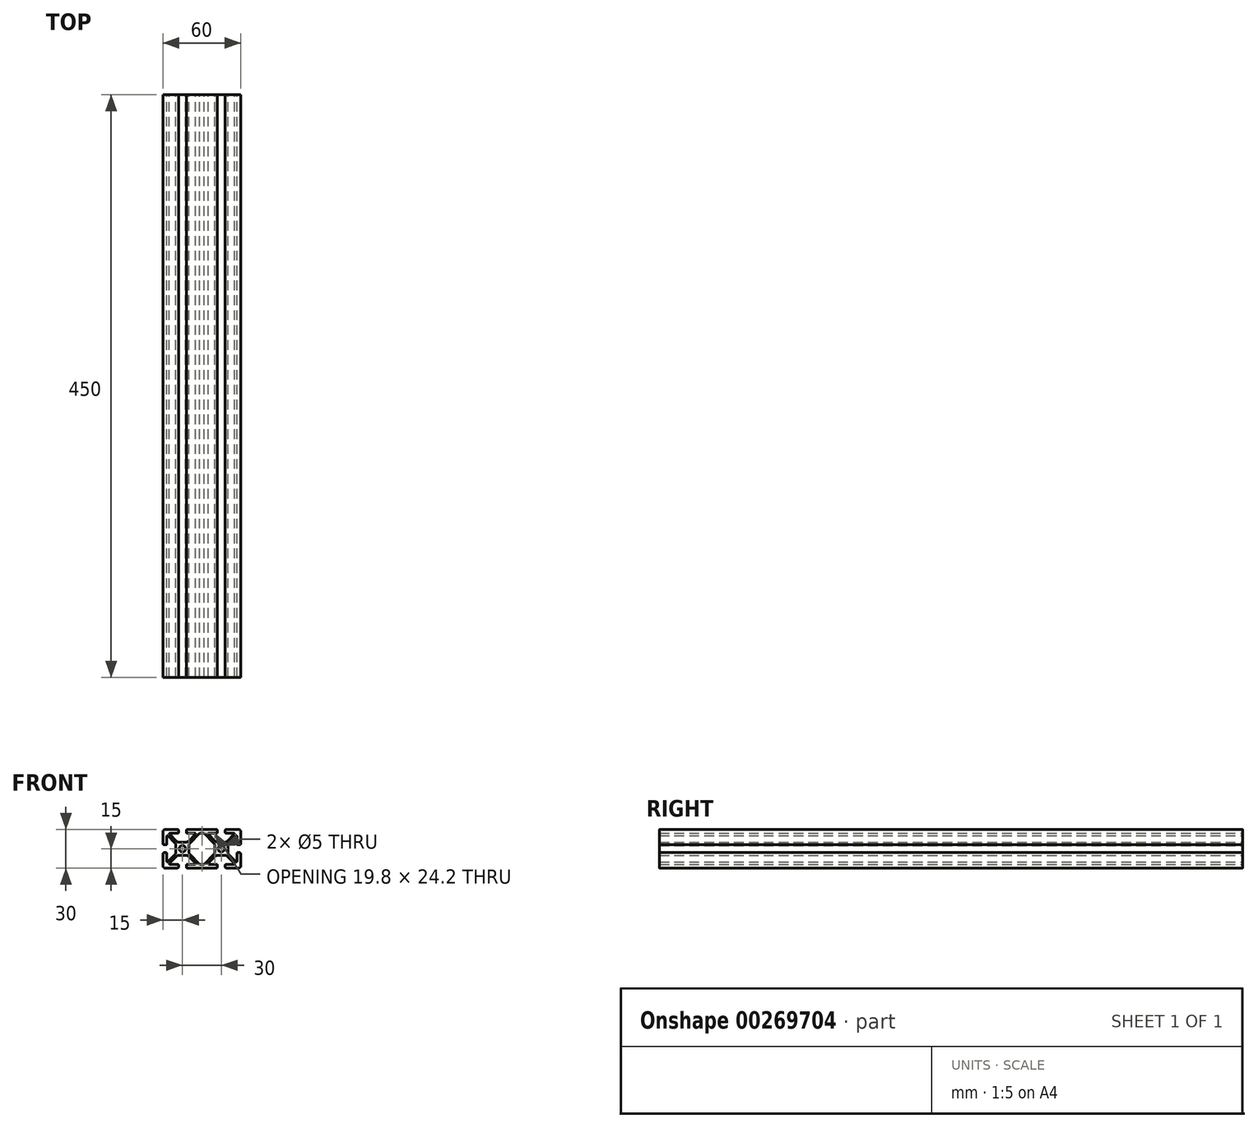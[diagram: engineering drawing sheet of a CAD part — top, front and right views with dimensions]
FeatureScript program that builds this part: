
annotation { "Feature Type Name" : "Feature", "Feature Type Description" : "" }
export const myFeature = defineFeature(function(context is Context, id is Id, definition is map)
    precondition{}
    {
        {
            var Q0;
            Q0=qCreatedBy(makeId("Front.planeOp"),FACE);
            var sketch = newSketch(context, id + "F0", { "sketchPlane" : qUnion([Q0])});
            skLineSegment(sketch, "E0.top", {"start": v(-28.2, -15) * mm, "end": v(-19, -15) * mm});
            skCircle(sketch, "E1", {"center": v(-15, 0) * mm, "radius": 2.5 * mm});
            skLineSegment(sketch, "E2", {"start": v(-15, 0) * mm, "end": v(15, 0) * mm, "construction": true});
            skLineSegment(sketch, "E3", {"start": v(-24.62, -12.1) * mm, "end": v(-18.5, -12.1) * mm});
            skLineSegment(sketch, "E4", {"start": v(-15, 0) * mm, "end": v(-15, -15) * mm, "construction": true});
            skLineSegment(sketch, "E5.bottom", {"start": v(-12.2, -5.1) * mm, "end": v(-17.8, -5.1) * mm});
            skLineSegment(sketch, "E6.trimOffspring", {"start": v(-18, -12.6) * mm, "end": v(-18, -14) * mm});
            skLineSegment(sketch, "E7.trimOffspring", {"start": v(-12, -12.6) * mm, "end": v(-12, -14) * mm});
            skLineSegment(sketch, "E8.trimOffspring", {"start": v(-11.5, -12.1) * mm, "end": v(-5.38, -12.1) * mm});
            skLineSegment(sketch, "E9.0", {"start": v(-26.25, -9.97) * mm, "end": v(-20.83, -4.56) * mm});
            skLineSegment(sketch, "E10.trimOffspring", {"start": v(-24.97, -11.25) * mm, "end": v(-19.56, -5.83) * mm});
            skLineSegment(sketch, "E11", {"start": v(-15, 0) * mm, "end": v(-30, -15) * mm, "construction": true});
            skLineSegment(sketch, "E12.MirrorCS", {"start": v(-27.1, -9.62) * mm, "end": v(-27.1, -3.5) * mm});
            skLineSegment(sketch, "E13.MirrorCS", {"start": v(-27.6, -3) * mm, "end": v(-29, -3) * mm});
            skLineSegment(sketch, "E14.MirrorCS", {"start": v(-5.03, -11.25) * mm, "end": v(-10.44, -5.83) * mm});
            skLineSegment(sketch, "E15.MirrorCS", {"start": v(-1.63, -12.1) * mm, "end": v(-9.17, -4.56) * mm});
            skLineSegment(sketch, "E16.trimOffspring", {"start": v(-30, -4) * mm, "end": v(-30, -13.2) * mm});
            skPoint(sketch, "E17.visualSharp", {"position": v(-30, -15) * mm});
            skArc(sketch, "E17.filletArc", {"start": v(-30, -13.2) * mm, "mid": v(-29.47, -14.47) * mm, "end": v(-28.2, -15) * mm});
            skPoint(sketch, "E18.visualSharp", {"position": v(-18, -15) * mm});
            skArc(sketch, "E18.filletArc", {"start": v(-19, -15) * mm, "mid": v(-18.3, -14.7) * mm, "end": v(-18, -14) * mm});
            skLineSegment(sketch, "E19", {"start": v(-18, -14) * mm, "end": v(-12, -14) * mm, "construction": true});
            skPoint(sketch, "E20", {"position": v(-15, -14) * mm});
            skPoint(sketch, "E21.orphan", {"position": v(-28.9, -5.1) * mm});
            skPoint(sketch, "E22.visualSharp", {"position": v(-18.83, -5.1) * mm});
            skArc(sketch, "E22.filletArc", {"start": v(-17.8, -5.1) * mm, "mid": v(-18.75, -5.3) * mm, "end": v(-19.56, -5.83) * mm});
            skPoint(sketch, "E23.visualSharp", {"position": v(-11.17, -5.1) * mm});
            skArc(sketch, "E23.filletArc", {"start": v(-10.44, -5.83) * mm, "mid": v(-11.25, -5.3) * mm, "end": v(-12.2, -5.1) * mm});
            skPoint(sketch, "E24.visualSharp", {"position": v(-23.4, -7.14) * mm});
            skArc(sketch, "E24.filletArc", {"start": v(-20.83, -4.56) * mm, "mid": v(-20.3, -3.75) * mm, "end": v(-20.1, -2.8) * mm});
            skPoint(sketch, "E25.visualSharp", {"position": v(-6.6, -7.14) * mm});
            skPoint(sketch, "E26.visualSharp", {"position": v(-12, -15) * mm});
            skArc(sketch, "E26.filletArc", {"start": v(-12, -14) * mm, "mid": v(-11.7, -14.7) * mm, "end": v(-11, -15) * mm});
            skPoint(sketch, "E27.visualSharp", {"position": v(-12, -12.1) * mm});
            skArc(sketch, "E27.filletArc", {"start": v(-11.5, -12.1) * mm, "mid": v(-11.85, -12.25) * mm, "end": v(-12, -12.6) * mm});
            skPoint(sketch, "E28.visualSharp", {"position": v(-18, -12.1) * mm});
            skArc(sketch, "E28.filletArc", {"start": v(-18, -12.6) * mm, "mid": v(-18.15, -12.25) * mm, "end": v(-18.5, -12.1) * mm});
            skPoint(sketch, "E29.visualSharp", {"position": v(-27.1, -3) * mm});
            skArc(sketch, "E29.filletArc", {"start": v(-27.1, -3.5) * mm, "mid": v(-27.25, -3.15) * mm, "end": v(-27.6, -3) * mm});
            skPoint(sketch, "E30.visualSharp", {"position": v(-30, -3) * mm});
            skArc(sketch, "E30.filletArc", {"start": v(-29, -3) * mm, "mid": v(-29.7, -3.3) * mm, "end": v(-30, -4) * mm});
            skPoint(sketch, "E31.visualSharp", {"position": v(-27.1, -10.83) * mm});
            skArc(sketch, "E31.filletArc", {"start": v(-27.1, -9.62) * mm, "mid": v(-26.8, -10.08) * mm, "end": v(-26.25, -9.97) * mm});
            skPoint(sketch, "E32.visualSharp", {"position": v(-25.83, -12.1) * mm});
            skArc(sketch, "E32.filletArc", {"start": v(-24.97, -11.25) * mm, "mid": v(-25.08, -11.8) * mm, "end": v(-24.62, -12.1) * mm});
            skPoint(sketch, "E33.visualSharp", {"position": v(-4.17, -12.1) * mm});
            skArc(sketch, "E33.filletArc", {"start": v(-5.38, -12.1) * mm, "mid": v(-4.92, -11.8) * mm, "end": v(-5.03, -11.25) * mm});
            skLineSegment(sketch, "E34", {"start": v(-10.44, 5.83) * mm, "end": v(-9.17, 4.56) * mm, "construction": true});
            skPoint(sketch, "E35", {"position": v(-9.8, 5.2) * mm});
            skLineSegment(sketch, "E36.MirrorCS", {"start": v(-28.2, 15) * mm, "end": v(-19, 15) * mm});
            skArc(sketch, "E37.MirrorCS", {"start": v(-30, 13.2) * mm, "mid": v(-29.47, 14.47) * mm, "end": v(-28.2, 15) * mm});
            skLineSegment(sketch, "E38.MirrorCS", {"start": v(-30, 4) * mm, "end": v(-30, 13.2) * mm});
            skArc(sketch, "E39.MirrorCS", {"start": v(-29, 3) * mm, "mid": v(-29.7, 3.3) * mm, "end": v(-30, 4) * mm});
            skLineSegment(sketch, "E40.MirrorCS", {"start": v(-27.6, 3) * mm, "end": v(-29, 3) * mm});
            skArc(sketch, "E41.MirrorCS", {"start": v(-27.1, 3.5) * mm, "mid": v(-27.25, 3.15) * mm, "end": v(-27.6, 3) * mm});
            skLineSegment(sketch, "E42.MirrorCS", {"start": v(-27.1, 9.62) * mm, "end": v(-27.1, 3.5) * mm});
            skArc(sketch, "E43.MirrorCS", {"start": v(-27.1, 9.62) * mm, "mid": v(-26.8, 10.08) * mm, "end": v(-26.25, 9.97) * mm});
            skLineSegment(sketch, "E44.MirrorCS", {"start": v(-26.25, 9.97) * mm, "end": v(-20.83, 4.56) * mm});
            skArc(sketch, "E45.MirrorCS", {"start": v(-20.83, 4.56) * mm, "mid": v(-20.3, 3.75) * mm, "end": v(-20.1, 2.8) * mm});
            skArc(sketch, "E46.MirrorCS", {"start": v(-19, 15) * mm, "mid": v(-18.3, 14.7) * mm, "end": v(-18, 14) * mm});
            skLineSegment(sketch, "E47.MirrorCS", {"start": v(-18, 12.6) * mm, "end": v(-18, 14) * mm});
            skArc(sketch, "E48.MirrorCS", {"start": v(-18, 12.6) * mm, "mid": v(-18.15, 12.25) * mm, "end": v(-18.5, 12.1) * mm});
            skLineSegment(sketch, "E49.MirrorCS", {"start": v(-24.62, 12.1) * mm, "end": v(-18.5, 12.1) * mm});
            skArc(sketch, "E50.MirrorCS", {"start": v(-24.97, 11.25) * mm, "mid": v(-25.08, 11.8) * mm, "end": v(-24.62, 12.1) * mm});
            skLineSegment(sketch, "E51.MirrorCS", {"start": v(-24.97, 11.25) * mm, "end": v(-19.56, 5.83) * mm});
            skArc(sketch, "E52.MirrorCS", {"start": v(-17.8, 5.1) * mm, "mid": v(-18.75, 5.3) * mm, "end": v(-19.56, 5.83) * mm});
            skLineSegment(sketch, "E53.MirrorCS", {"start": v(-12.2, 5.1) * mm, "end": v(-17.8, 5.1) * mm});
            skArc(sketch, "E54.MirrorCS", {"start": v(-10.44, 5.83) * mm, "mid": v(-11.25, 5.3) * mm, "end": v(-12.2, 5.1) * mm});
            skLineSegment(sketch, "E55.MirrorCS", {"start": v(-5.03, 11.25) * mm, "end": v(-10.44, 5.83) * mm});
            skArc(sketch, "E56.MirrorCS", {"start": v(-5.38, 12.1) * mm, "mid": v(-4.92, 11.8) * mm, "end": v(-5.03, 11.25) * mm});
            skLineSegment(sketch, "E57.MirrorCS", {"start": v(-11.5, 12.1) * mm, "end": v(-5.38, 12.1) * mm});
            skArc(sketch, "E58.MirrorCS", {"start": v(-11.5, 12.1) * mm, "mid": v(-11.85, 12.25) * mm, "end": v(-12, 12.6) * mm});
            skLineSegment(sketch, "E59.MirrorCS", {"start": v(-12, 12.6) * mm, "end": v(-12, 14) * mm});
            skArc(sketch, "E60.MirrorCS", {"start": v(-12, 14) * mm, "mid": v(-11.7, 14.7) * mm, "end": v(-11, 15) * mm});
            skLineSegment(sketch, "E61.MirrorCS", {"start": v(-1.63, 12.1) * mm, "end": v(-9.17, 4.56) * mm});
            skLineSegment(sketch, "E62", {"start": v(-20.1, -2.8) * mm, "end": v(-20.1, 2.8) * mm});
            skLineSegment(sketch, "E63", {"start": v(-9.9, 2.8) * mm, "end": v(-9.9, -2.8) * mm});
            skPoint(sketch, "E64.visualSharp", {"position": v(-1.63, 12.1) * mm});
            skPoint(sketch, "E65.visualSharp", {"position": v(-1.63, -12.1) * mm});
            skLineSegment(sketch, "E66", {"start": v(-11, -15) * mm, "end": v(0, -15) * mm});
            skLineSegment(sketch, "E67.MirrorCS", {"start": v(-11, 15) * mm, "end": v(0, 15) * mm});
            skLineSegment(sketch, "E68", {"start": v(-1.63, 12.1) * mm, "end": v(0, 12.1) * mm});
            skLineSegment(sketch, "E69", {"start": v(-1.63, -12.1) * mm, "end": v(0, -12.1) * mm});
            skPoint(sketch, "E70.visualSharp", {"position": v(-9.9, 3.83) * mm});
            skArc(sketch, "E70.filletArc", {"start": v(-9.17, 4.56) * mm, "mid": v(-9.7, 3.75) * mm, "end": v(-9.9, 2.8) * mm});
            skPoint(sketch, "E71.visualSharp", {"position": v(-9.9, -3.83) * mm});
            skArc(sketch, "E71.filletArc", {"start": v(-9.9, -2.8) * mm, "mid": v(-9.7, -3.75) * mm, "end": v(-9.17, -4.56) * mm});
            skLineSegment(sketch, "E72", {"start": v(0, 15) * mm, "end": v(0, 12.1) * mm});
            skLineSegment(sketch, "E73", {"start": v(0, -12.1) * mm, "end": v(0, -15) * mm});
            skSolve(sketch);
        }
        {
            var Q0;
            Q0=makeQuery(id+"F0.imprint","IMPRINT",FACE,{"disambiguationData":[TD([[makeQuery(id+"F0.imprint","IMPRINT",EDGE,{"derivedFrom":sQuery(id+"F0.wireOp",EDGE,"E0.top")}),1.0]])]});
            extrude(context, id + "F1", {"entities" : qUnion([Q0]), "depth" : 450 * mm});
        }
        {
            var Q0;
            Q0=makeQuery(id+"F1.opExtrude","SWEPT_BODY",BODY,{"disambiguationData":[OSD([sQuery(id+"F0.wireOp",EDGE,"E0.top"),sQuery(id+"F0.wireOp",EDGE,"E1"),sQuery(id+"F0.wireOp",EDGE,"xx0pEBMj-jRSv-Lbnr-q3nJ-SJRiq3M36ffO"),sQuery(id+"F0.wireOp",EDGE,"E3"),sQuery(id+"F0.wireOp",EDGE,"E5.bottom"),sQuery(id+"F0.wireOp",EDGE,"E6.trimOffspring"),sQuery(id+"F0.wireOp",EDGE,"E7.trimOffspring"),sQuery(id+"F0.wireOp",EDGE,"E8.trimOffspring"),sQuery(id+"F0.wireOp",EDGE,"E9.0"),sQuery(id+"F0.wireOp",EDGE,"E10.trimOffspring"),sQuery(id+"F0.wireOp",EDGE,"E12.MirrorCS"),sQuery(id+"F0.wireOp",EDGE,"E13.MirrorCS"),sQuery(id+"F0.wireOp",EDGE,"E14.MirrorCS"),sQuery(id+"F0.wireOp",EDGE,"E15.MirrorCS"),sQuery(id+"F0.wireOp",EDGE,"E16.trimOffspring"),sQuery(id+"F0.wireOp",EDGE,"E17.filletArc"),sQuery(id+"F0.wireOp",EDGE,"E18.filletArc"),sQuery(id+"F0.wireOp",EDGE,"E22.filletArc"),sQuery(id+"F0.wireOp",EDGE,"E23.filletArc"),sQuery(id+"F0.wireOp",EDGE,"E24.filletArc"),sQuery(id+"F0.wireOp",EDGE,"E25.filletArc"),sQuery(id+"F0.wireOp",EDGE,"E26.filletArc"),sQuery(id+"F0.wireOp",EDGE,"E27.filletArc"),sQuery(id+"F0.wireOp",EDGE,"E28.filletArc"),sQuery(id+"F0.wireOp",EDGE,"E29.filletArc"),sQuery(id+"F0.wireOp",EDGE,"E30.filletArc"),sQuery(id+"F0.wireOp",EDGE,"E31.filletArc"),sQuery(id+"F0.wireOp",EDGE,"E32.filletArc"),sQuery(id+"F0.wireOp",EDGE,"E33.filletArc"),sQuery(id+"F0.wireOp",EDGE,"E36.MirrorCS"),sQuery(id+"F0.wireOp",EDGE,"E37.MirrorCS"),sQuery(id+"F0.wireOp",EDGE,"E38.MirrorCS"),sQuery(id+"F0.wireOp",EDGE,"E39.MirrorCS"),sQuery(id+"F0.wireOp",EDGE,"E40.MirrorCS"),sQuery(id+"F0.wireOp",EDGE,"E41.MirrorCS"),sQuery(id+"F0.wireOp",EDGE,"E42.MirrorCS"),sQuery(id+"F0.wireOp",EDGE,"E43.MirrorCS"),sQuery(id+"F0.wireOp",EDGE,"E44.MirrorCS"),sQuery(id+"F0.wireOp",EDGE,"E45.MirrorCS"),sQuery(id+"F0.wireOp",EDGE,"E46.MirrorCS"),sQuery(id+"F0.wireOp",EDGE,"E47.MirrorCS"),sQuery(id+"F0.wireOp",EDGE,"E48.MirrorCS"),sQuery(id+"F0.wireOp",EDGE,"E49.MirrorCS"),sQuery(id+"F0.wireOp",EDGE,"E50.MirrorCS"),sQuery(id+"F0.wireOp",EDGE,"E51.MirrorCS"),sQuery(id+"F0.wireOp",EDGE,"E52.MirrorCS"),sQuery(id+"F0.wireOp",EDGE,"E53.MirrorCS"),sQuery(id+"F0.wireOp",EDGE,"E54.MirrorCS"),sQuery(id+"F0.wireOp",EDGE,"E55.MirrorCS"),sQuery(id+"F0.wireOp",EDGE,"E56.MirrorCS"),sQuery(id+"F0.wireOp",EDGE,"E57.MirrorCS"),sQuery(id+"F0.wireOp",EDGE,"E58.MirrorCS"),sQuery(id+"F0.wireOp",EDGE,"E59.MirrorCS"),sQuery(id+"F0.wireOp",EDGE,"E60.MirrorCS"),sQuery(id+"F0.wireOp",EDGE,"E61.MirrorCS"),sQuery(id+"F0.wireOp",EDGE,"84e0606f-2660-47d3-8066-1f6780e61d240.MirrorCS"),sQuery(id+"F0.wireOp",EDGE,"E62"),sQuery(id+"F0.wireOp",EDGE,"E63"),sQuery(id+"F0.wireOp",EDGE,"8777beac-d77c-45ca-af0e-820e461171390.MirrorCS"),sQuery(id+"F0.wireOp",EDGE,"8777beac-d77c-45ca-af0e-820e461171391.MirrorCS"),sQuery(id+"F0.wireOp",EDGE,"8777beac-d77c-45ca-af0e-820e461171393.MirrorCS"),sQuery(id+"F0.wireOp",EDGE,"8777beac-d77c-45ca-af0e-820e461171395.MirrorCS"),sQuery(id+"F0.wireOp",EDGE,"2eeeb882-eed5-4166-8e1e-a32fedb74f402.MirrorCS"),sQuery(id+"F0.wireOp",EDGE,"2eeeb882-eed5-4166-8e1e-a32fedb74f404.MirrorCS"),sQuery(id+"F0.wireOp",EDGE,"c7ab986a-4e71-4e94-875b-888b0b74b8760.MirrorCS"),sQuery(id+"F0.wireOp",EDGE,"30fd93c4-a74a-4645-b8f2-30fa4af6f5170.MirrorCS"),sQuery(id+"F0.wireOp",EDGE,"30fd93c4-a74a-4645-b8f2-30fa4af6f5171.MirrorCS"),sQuery(id+"F0.wireOp",EDGE,"30fd93c4-a74a-4645-b8f2-30fa4af6f5173.MirrorCS"),sQuery(id+"F0.wireOp",EDGE,"30fd93c4-a74a-4645-b8f2-30fa4af6f5174.MirrorCS"),sQuery(id+"F0.wireOp",EDGE,"30fd93c4-a74a-4645-b8f2-30fa4af6f5176.MirrorCS"),sQuery(id+"F0.wireOp",EDGE,"30fd93c4-a74a-4645-b8f2-30fa4af6f5177.MirrorCS"),sQuery(id+"F0.wireOp",EDGE,"30fd93c4-a74a-4645-b8f2-30fa4af6f5178.MirrorCS"),sQuery(id+"F0.wireOp",EDGE,"30fd93c4-a74a-4645-b8f2-30fa4af6f5179.MirrorCS"),sQuery(id+"F0.wireOp",EDGE,"c75a34bd-beff-4123-8e26-f2b4586136f20.MirrorCS"),sQuery(id+"F0.wireOp",EDGE,"d07f147f-3e59-4fec-a451-0a70723a730d0.MirrorCS"),sQuery(id+"F0.wireOp",EDGE,"25a2e1f4-fbdf-476f-b2df-d9d4e9416ce50.MirrorCS"),sQuery(id+"F0.wireOp",EDGE,"54c044ec-2a1f-477a-a750-c40de18a63860.MirrorCS"),sQuery(id+"F0.wireOp",EDGE,"e7b3a241-c0a6-4482-8933-493674b3ba2e0.MirrorCS"),sQuery(id+"F0.wireOp",EDGE,"564d2562-e668-4c5a-a657-de88a3b70ec20.MirrorCS"),sQuery(id+"F0.wireOp",EDGE,"NHzEeUZn-j6aY-zjJj-DU6j-r29A23V1wuZp"),sQuery(id+"F0.wireOp",EDGE,"euIQqrrk-acdu-msLV-AXC1-f6gACNh7W0Cw"),sQuery(id+"F0.wireOp",EDGE,"E64.filletArc"),sQuery(id+"F0.wireOp",EDGE,"d731a9ce-1f9b-403d-a03f-e33f864c1e18.filletArc"),sQuery(id+"F0.wireOp",EDGE,"E65.filletArc"),sQuery(id+"F0.wireOp",EDGE,"63dcdacc-e304-4e1a-9721-d4ad0a47304f.filletArc"),sQuery(id+"F0.wireOp",EDGE,"35acc7aa-d704-43ea-868f-18a7ec3bdda70.MirrorCS"),sQuery(id+"F0.wireOp",EDGE,"fd040732-486b-4390-b425-ec4351d0e7e80.MirrorCS"),sQuery(id+"F0.wireOp",EDGE,"e578b67e-7911-4d93-92d3-7d22e9965f8e0.MirrorCS"),sQuery(id+"F0.wireOp",EDGE,"7a2807d8-86e2-4767-a200-7e81fd7f1f560.MirrorCS"),sQuery(id+"F0.wireOp",EDGE,"678a208d-c2a0-4aa2-b562-dc4c6234dfb40.MirrorCS"),sQuery(id+"F0.wireOp",EDGE,"f93236e3-4b4b-4808-aea5-9cdb7003f4050.MirrorCS"),sQuery(id+"F0.wireOp",EDGE,"0abef614-89f8-45e5-ac6e-1a178c9fc8b00.MirrorCS"),sQuery(id+"F0.wireOp",EDGE,"684fc782-96a6-47d3-a8c4-6e3182d5f3880.MirrorCS"),sQuery(id+"F0.wireOp",EDGE,"ae1c2d55-bc04-4e60-877a-dd5b8da22af00.MirrorCS"),sQuery(id+"F0.wireOp",EDGE,"662c4d57-50f4-4984-86b3-1351e2e6145b0.MirrorCS"),sQuery(id+"F0.wireOp",EDGE,"35bb1620-225b-454e-ac61-06da3b6371ea0.MirrorCS"),sQuery(id+"F0.wireOp",EDGE,"98add64f-431e-44f0-bccb-54f6e294647c0.MirrorCS"),sQuery(id+"F0.wireOp",EDGE,"13160950-3bda-40c9-b6f8-cbba89ccfef70.MirrorCS"),sQuery(id+"F0.wireOp",EDGE,"6be86dc8-a880-4c35-bcdf-8b3f5eee2cdd0.MirrorCS"),sQuery(id+"F0.wireOp",EDGE,"484c263f-cc48-46be-8847-f486bbebeede0.MirrorCS"),sQuery(id+"F0.wireOp",EDGE,"5f8588aa-2e83-4b97-b956-8e531a4eb46d0.MirrorCS"),sQuery(id+"F0.wireOp",EDGE,"2d822380-6e79-4d37-84ac-f398f3e25ab50.MirrorCS"),sQuery(id+"F0.wireOp",EDGE,"E66"),sQuery(id+"F0.wireOp",EDGE,"3SnkwM6S-Ex2K-kpp2-J1OZ-N5tMk4ROZJVr"),sQuery(id+"F0.wireOp",EDGE,"02575252-a9dd-4ab6-bd93-705c5555701e0.MirrorCS"),sQuery(id+"F0.wireOp",EDGE,"E67.MirrorCS"),sQuery(id+"F0.wireOp",EDGE,"66fab678-6442-4b16-833e-680aac1342370.MirrorCS"),sQuery(id+"F0.wireOp",EDGE,"d2d66b98-cc5c-436b-9ced-b73637c72f690.MirrorCS"),sQuery(id+"F0.wireOp",EDGE,"095b0e8a-5b2c-452e-882b-1944bbcbc7fe0.MirrorCS"),sQuery(id+"F0.wireOp",EDGE,"df691f2d-5f11-4f57-8a33-bca0a1592ec30.MirrorCS"),sQuery(id+"F0.wireOp",EDGE,"a2a9021a-c8e0-4c9d-9d7a-1de230806d980.MirrorCS"),sQuery(id+"F0.wireOp",EDGE,"ad83d616-585a-48a3-b278-d4401a45ed7e0.MirrorCS"),sQuery(id+"F0.wireOp",EDGE,"0347e20a-31d5-45e7-a402-947e340792340.MirrorCS"),sQuery(id+"F0.wireOp",EDGE,"5deaee7e-06ea-4911-bed0-68f2c0d7f7c50.MirrorCS"),sQuery(id+"F0.wireOp",EDGE,"zOQuU1W7-kDfO-8kRA-MtJh-F7DlEQ6mTgwY"),sQuery(id+"F0.wireOp",EDGE,"FsaTKIVf-019f-RWmk-kc5g-H0LFoSPPNp8z")])]});
            var Q1;
            Q1=qCreatedBy(makeId("Right.planeOp"),FACE);
            mirror(context, id + "F2", {"operationType" : NewBodyOperationType.ADD, "entities" : qUnion([Q0]), "mirrorPlane" : qUnion([Q1])});
        }
    });
